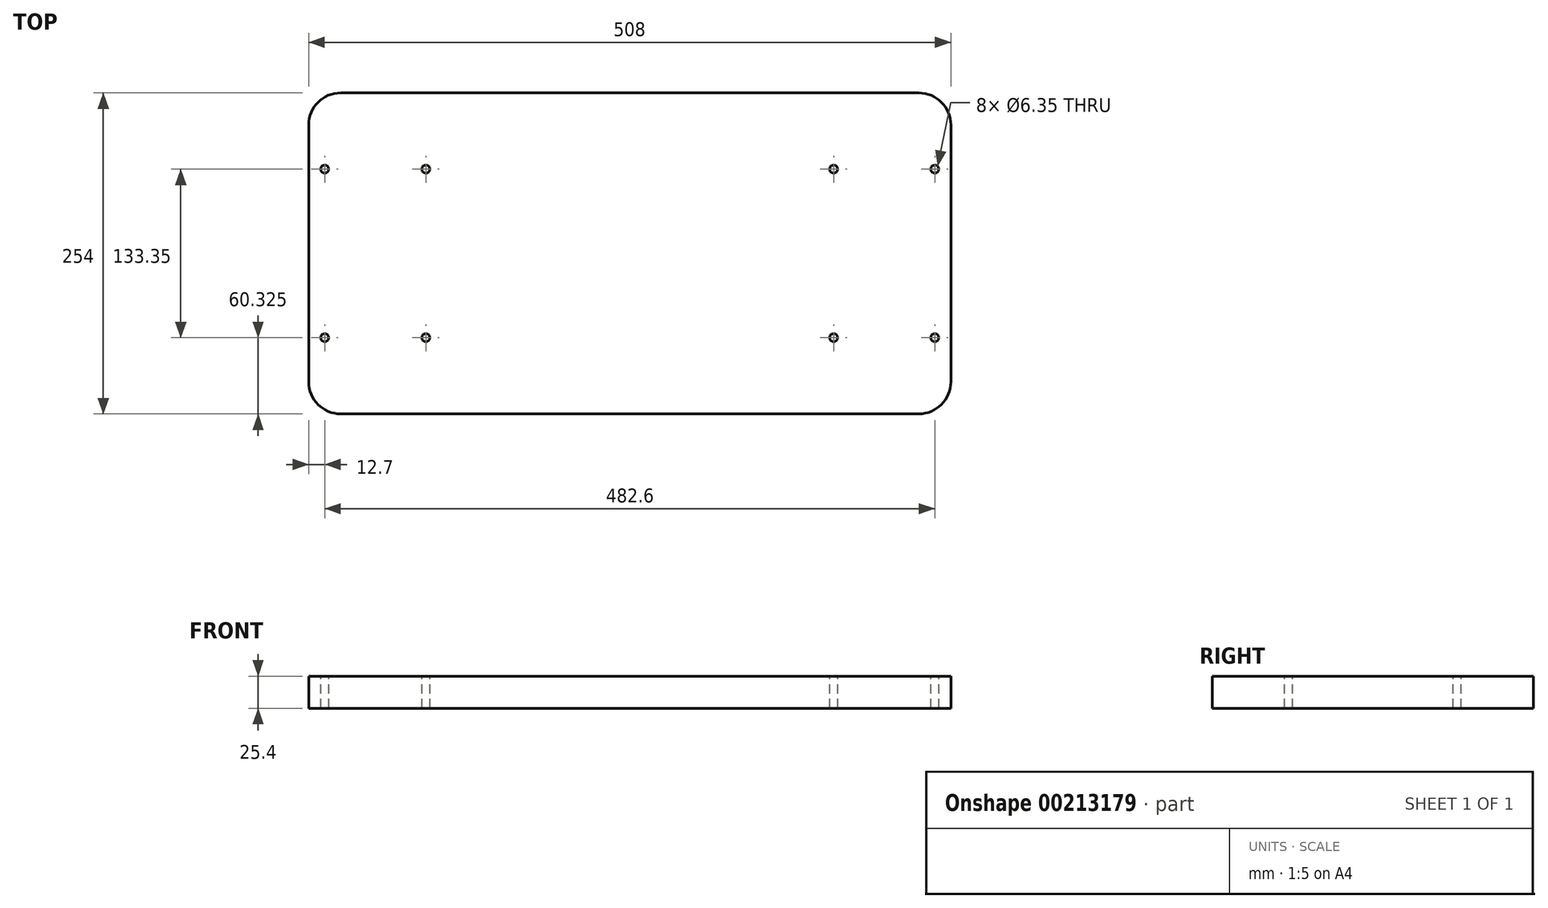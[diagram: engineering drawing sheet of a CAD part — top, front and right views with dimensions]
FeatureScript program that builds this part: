
annotation { "Feature Type Name" : "Feature", "Feature Type Description" : "" }
export const myFeature = defineFeature(function(context is Context, id is Id, definition is map)
    precondition{}
    {
        {
            var Q0;
            Q0=qCreatedBy(makeId("Top.planeOp"),FACE);
            var sketch = newSketch(context, id + "F0", { "sketchPlane" : qUnion([Q0])});
            skLineSegment(sketch, "E0", {"start": v(25.4, 0) * mm, "end": v(482.6, 0) * mm});
            skLineSegment(sketch, "E1", {"start": v(508, 25.4) * mm, "end": v(508, 228.6) * mm});
            skLineSegment(sketch, "E2", {"start": v(482.6, 254) * mm, "end": v(25.4, 254) * mm});
            skLineSegment(sketch, "E3", {"start": v(0, 228.6) * mm, "end": v(0, 25.4) * mm});
            skPoint(sketch, "E4.visualSharp", {"position": v(0, 254) * mm});
            skArc(sketch, "E4.filletArc", {"start": v(25.4, 254) * mm, "mid": v(7.44, 246.56) * mm, "end": v(0, 228.6) * mm});
            skPoint(sketch, "E5.visualSharp", {"position": v(508, 254) * mm});
            skArc(sketch, "E5.filletArc", {"start": v(508, 228.6) * mm, "mid": v(500.56, 246.56) * mm, "end": v(482.6, 254) * mm});
            skPoint(sketch, "E6.visualSharp", {"position": v(508, 0) * mm});
            skArc(sketch, "E6.filletArc", {"start": v(482.6, 0) * mm, "mid": v(500.56, 7.44) * mm, "end": v(508, 25.4) * mm});
            skPoint(sketch, "E7.visualSharp", {"position": v(0, 0) * mm});
            skArc(sketch, "E7.filletArc", {"start": v(0, 25.4) * mm, "mid": v(7.44, 7.44) * mm, "end": v(25.4, 0) * mm});
            skSolve(sketch);
        }
        {
            var Q0;
            Q0=makeQuery(id+"F0.imprint","IMPRINT",FACE,{"disambiguationData":[TD([[makeQuery(id+"F0.imprint","IMPRINT",EDGE,{"derivedFrom":sQuery(id+"F0.wireOp",EDGE,"E0")}),1.0]])]});
            extrude(context, id + "F1", {"entities" : qUnion([Q0]), "depth" : 25.4 * mm});
        }
        {
            var Q0;
            Q0=makeQuery(id+"F1.opExtrude","CAP_FACE",FACE,{"disambiguationData":[OSD([sQuery(id+"F0.wireOp",EDGE,"E0"),sQuery(id+"F0.wireOp",EDGE,"E1"),sQuery(id+"F0.wireOp",EDGE,"E2"),sQuery(id+"F0.wireOp",EDGE,"E3"),sQuery(id+"F0.wireOp",EDGE,"E4.filletArc"),sQuery(id+"F0.wireOp",EDGE,"E5.filletArc"),sQuery(id+"F0.wireOp",EDGE,"E6.filletArc"),sQuery(id+"F0.wireOp",EDGE,"E7.filletArc")])],"isStart":false});
            var sketch = newSketch(context, id + "F2", { "sketchPlane" : qUnion([Q0])});
            skLineSegment(sketch, "E8", {"start": v(-4.57, 127) * mm, "end": v(531.4, 127) * mm, "construction": true});
            skLineSegment(sketch, "E9", {"start": v(254, 292.93) * mm, "end": v(254, -41.05) * mm, "construction": true});
            skPoint(sketch, "E10", {"position": v(12.7, 193.68) * mm});
            skPoint(sketch, "E11", {"position": v(92.71, 193.68) * mm});
            skPoint(sketch, "E12", {"position": v(0, 192.49) * mm});
            skPoint(sketch, "E13.MirrorP", {"position": v(92.71, 60.33) * mm});
            skPoint(sketch, "E14.MirrorP", {"position": v(12.7, 60.32) * mm});
            skPoint(sketch, "E15.MirrorP", {"position": v(415.29, 193.68) * mm});
            skPoint(sketch, "E16.MirrorP", {"position": v(495.3, 193.68) * mm});
            skPoint(sketch, "E17.MirrorP", {"position": v(415.29, 60.33) * mm});
            skPoint(sketch, "E18.MirrorP", {"position": v(495.3, 60.32) * mm});
            skSolve(sketch);
        }
        {
            var Q0;
            Q0=sQuery(id+"F2.wireOp",VERTEX,"E10");
            var Q1;
            Q1=sQuery(id+"F2.wireOp",VERTEX,"E11");
            var Q2;
            Q2=sQuery(id+"F2.wireOp",VERTEX,"E13.MirrorP");
            var Q3;
            Q3=sQuery(id+"F2.wireOp",VERTEX,"E14.MirrorP");
            var Q4;
            Q4=sQuery(id+"F2.wireOp",VERTEX,"E17.MirrorP");
            var Q5;
            Q5=sQuery(id+"F2.wireOp",VERTEX,"E18.MirrorP");
            var Q6;
            Q6=sQuery(id+"F2.wireOp",VERTEX,"E16.MirrorP");
            var Q7;
            Q7=sQuery(id+"F2.wireOp",VERTEX,"E15.MirrorP");
            var Q8;
            Q8=makeQuery(id+"F1.opExtrude","SWEPT_BODY",BODY,{"disambiguationData":[OSD([sQuery(id+"F0.wireOp",EDGE,"E0"),sQuery(id+"F0.wireOp",EDGE,"E1"),sQuery(id+"F0.wireOp",EDGE,"E2"),sQuery(id+"F0.wireOp",EDGE,"E3"),sQuery(id+"F0.wireOp",EDGE,"E4.filletArc"),sQuery(id+"F0.wireOp",EDGE,"E5.filletArc"),sQuery(id+"F0.wireOp",EDGE,"E6.filletArc"),sQuery(id+"F0.wireOp",EDGE,"E7.filletArc")])]});
            hole(context, id + "F3", {"style" : HoleStyle.SIMPLE, "endStyle" : HoleEndStyle.THROUGH, "holeDiameter" : 6.35 * mm, "locations" : qUnion([Q0, Q1, Q2, Q3, Q4, Q5, Q6, Q7]), "scope" : qUnion([Q8]), "isTappedThrough" : true});
        }
    });
